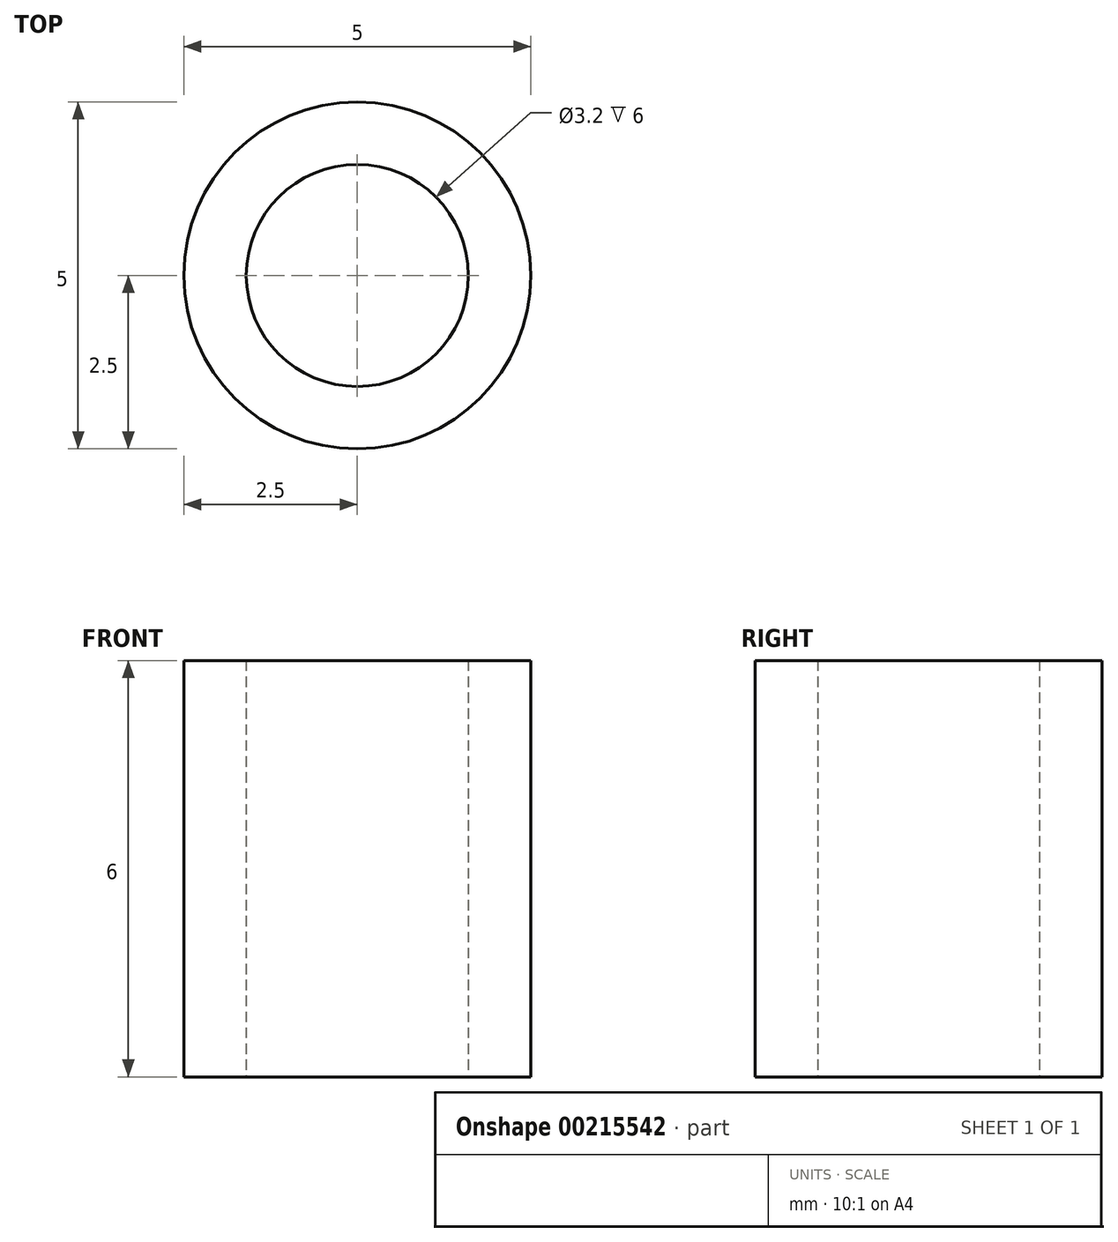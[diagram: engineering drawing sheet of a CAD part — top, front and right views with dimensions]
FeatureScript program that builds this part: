
annotation { "Feature Type Name" : "Feature", "Feature Type Description" : "" }
export const myFeature = defineFeature(function(context is Context, id is Id, definition is map)
    precondition{}
    {
        {
            var Q0;
            Q0=qCreatedBy(makeId("Top.planeOp"),FACE);
            var sketch = newSketch(context, id + "F0", { "sketchPlane" : qUnion([Q0])});
            skCircle(sketch, "E0", {"center": v(0, 0) * mm, "radius": 1.6 * mm});
            skCircle(sketch, "E1", {"center": v(0, 0) * mm, "radius": 2.5 * mm});
            skSolve(sketch);
        }
        {
            var Q0;
            Q0 = qSketchRegion(id + "F0", true);
            extrude(context, id + "F1", {"entities" : qUnion([Q0]), "depth" : 6 * mm});
        }
    });
